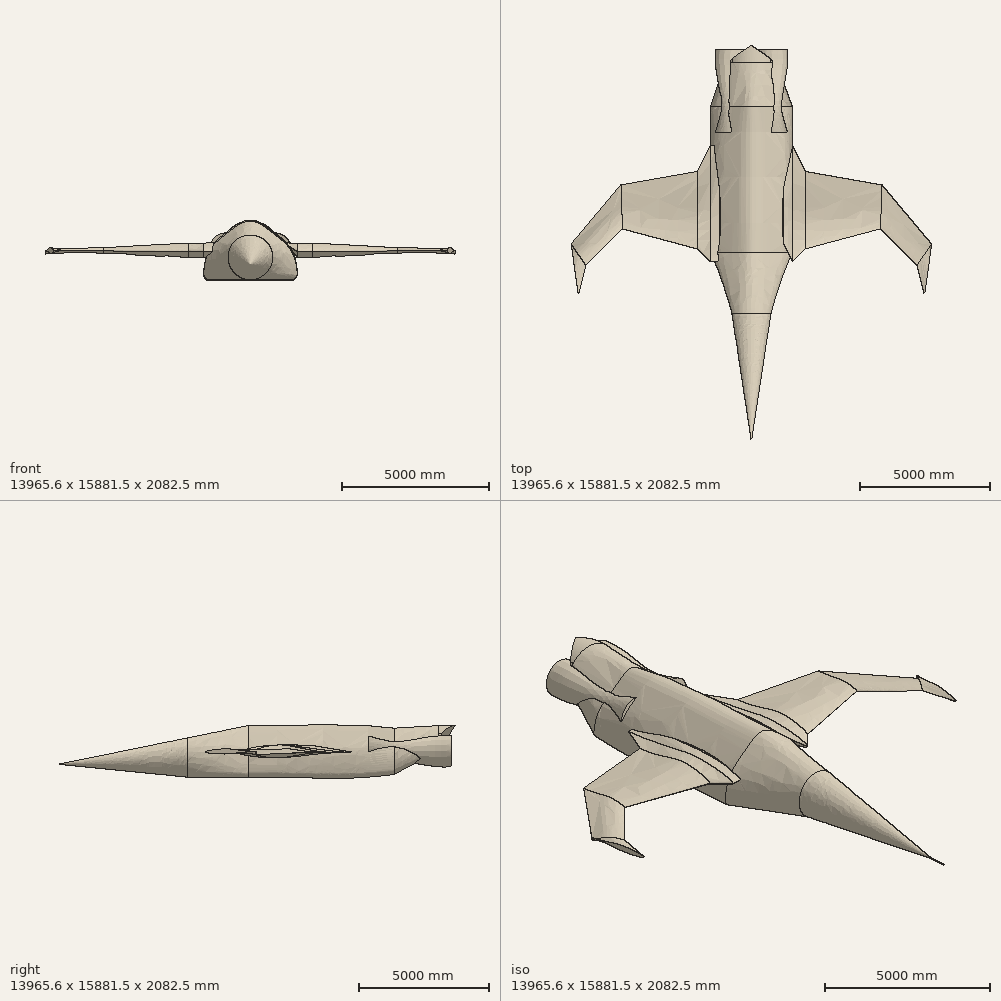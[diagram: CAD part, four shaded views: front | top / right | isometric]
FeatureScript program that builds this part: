
annotation { "Feature Type Name" : "Feature", "Feature Type Description" : "" }
export const myFeature = defineFeature(function(context is Context, id is Id, definition is map)
    precondition{}
    {
        {
            var Q0;
            Q0=qCreatedBy(makeId("Right.planeOp"),FACE);
            var sketch = newSketch(context, id + "F0", { "sketchPlane" : qUnion([Q0])});
            skLineSegment(sketch, "E0", {"start": v(0, 0) * mm, "end": v(-1750, 0) * mm});
            skLineSegment(sketch, "E1", {"start": v(-1750, 0) * mm, "end": v(-3500, 0) * mm});
            skLineSegment(sketch, "E2", {"start": v(-3500, 0) * mm, "end": v(-3500, -1000) * mm});
            skLineSegment(sketch, "E3", {"start": v(-3500, -1000) * mm, "end": v(-8500, -1000) * mm});
            skLineSegment(sketch, "E4", {"start": v(-8500, -1000) * mm, "end": v(-8500, -499.31) * mm});
            skLineSegment(sketch, "E5", {"start": v(-1151.4, 0) * mm, "end": v(-1151.4, 1000) * mm});
            skLineSegment(sketch, "E6", {"start": v(-1151.4, 1000) * mm, "end": v(-8500, -499.31) * mm});
            skLineSegment(sketch, "E7", {"start": v(-8500, -499.31) * mm, "end": v(-3500, -1000) * mm});
            skLineSegment(sketch, "E8", {"start": v(-3500, 0) * mm, "end": v(-3500, 520.82) * mm});
            skLineSegment(sketch, "E9", {"start": v(-8500, -499.31) * mm, "end": v(-8450, -499.31) * mm});
            skLineSegment(sketch, "E10", {"start": v(-8450, -499.31) * mm, "end": v(-8450, -489.1) * mm});
            skLineSegment(sketch, "E11", {"start": v(-8450, -499.31) * mm, "end": v(-8450, -504.32) * mm});
            skSolve(sketch);
        }
        {
            var Q0;
            Q0=sQuery(id+"F0.wireOp",EDGE,"E5");
            cPlane(context, id + "F1", {"entities" : qUnion([Q0]), "cplaneType" : CPlaneType.LINE_ANGLE, "offset" : 25 * mm, "angle" : 90 * degree, "oppositeDirection" : true, "width" : 150 * mm, "height" : 150 * mm});
        }
        {
            var Q0;
            Q0=qCreatedBy(id+"F1.planeOp",FACE);
            var sketch = newSketch(context, id + "F2", { "sketchPlane" : qUnion([Q0])});
            skLineSegment(sketch, "E12.top", {"start": v(-1394.2, -1000) * mm, "end": v(1394.2, -1000) * mm});
            skPoint(sketch, "E12.middle", {"position": v(0, 0) * mm});
            skFitSpline(sketch, "E13", {"points": [v(-1600, -1000) * mm, v(-848, 530) * mm, v(0, 1000) * mm, v(848, 530) * mm, v(1600, -1000) * mm], "startDerivative": vector(0, 10524.75) * mm, "endDerivative": vector(0, -10524.75) * mm});
            skArc(sketch, "E14", {"start": v(-735.27, 618.52) * mm, "mid": v(-1273.27, 435.52) * mm, "end": v(-1440.68, -107.53) * mm});
            skArc(sketch, "E15", {"start": v(1440.68, -107.53) * mm, "mid": v(1273.27, 435.52) * mm, "end": v(735.27, 618.52) * mm});
            skFitSpline(sketch, "E16.trimOffspring", {"points": [v(-1600, -1000) * mm, v(-848, 530) * mm, v(0, 1000) * mm, v(848, 530) * mm, v(1600, -1000) * mm], "startDerivative": vector(0, 10524.75) * mm, "endDerivative": vector(0, -10524.75) * mm});
            skFitSpline(sketch, "E17.trimOffspring", {"points": [v(-1600, -1000) * mm, v(-848, 530) * mm, v(0, 1000) * mm, v(848, 530) * mm, v(1600, -1000) * mm], "startDerivative": vector(0, 10524.75) * mm, "endDerivative": vector(0, -10524.75) * mm});
            skArc(sketch, "E18.filletArc", {"start": v(-1593.82, -787.83) * mm, "mid": v(-1539.85, -937.05) * mm, "end": v(-1394.2, -1000) * mm});
            skArc(sketch, "E19.filletArc", {"start": v(1394.2, -1000) * mm, "mid": v(1539.85, -937.05) * mm, "end": v(1593.82, -787.83) * mm});
            skSolve(sketch);
        }
        {
            var Q0;
            Q0=qCreatedBy(makeId("Front.planeOp"),FACE);
            var sketch = newSketch(context, id + "F3", { "sketchPlane" : qUnion([Q0])});
            skLineSegment(sketch, "E20.top", {"start": v(-1394.2, -1000) * mm, "end": v(1394.2, -1000) * mm});
            skPoint(sketch, "E20.middle", {"position": v(0, 0) * mm});
            skFitSpline(sketch, "E21", {"points": [v(-1600, -1000) * mm, v(-848, 530) * mm, v(0, 1000) * mm, v(848, 530) * mm, v(1600, -1000) * mm], "startDerivative": vector(0, 10524.75) * mm, "endDerivative": vector(0, -10524.75) * mm});
            skArc(sketch, "E22", {"start": v(-735.27, 618.52) * mm, "mid": v(-1273.27, 435.52) * mm, "end": v(-1440.68, -107.53) * mm});
            skArc(sketch, "E23", {"start": v(1440.68, -107.53) * mm, "mid": v(1273.27, 435.52) * mm, "end": v(735.27, 618.52) * mm});
            skFitSpline(sketch, "E24.trimOffspring", {"points": [v(-1600, -1000) * mm, v(-848, 530) * mm, v(0, 1000) * mm, v(848, 530) * mm, v(1600, -1000) * mm], "startDerivative": vector(0, 10524.75) * mm, "endDerivative": vector(0, -10524.75) * mm});
            skFitSpline(sketch, "E25.trimOffspring", {"points": [v(-1600, -1000) * mm, v(-848, 530) * mm, v(0, 1000) * mm, v(848, 530) * mm, v(1600, -1000) * mm], "startDerivative": vector(0, 10524.75) * mm, "endDerivative": vector(0, -10524.75) * mm});
            skArc(sketch, "E26.filletArc", {"start": v(-1593.82, -787.83) * mm, "mid": v(-1539.85, -937.05) * mm, "end": v(-1394.2, -1000) * mm});
            skArc(sketch, "E27.filletArc", {"start": v(1394.2, -1000) * mm, "mid": v(1539.85, -937.05) * mm, "end": v(1593.82, -787.83) * mm});
            skSolve(sketch);
        }
        {
            var Q0;
            Q0=qCreatedBy(makeId("Front.planeOp"),FACE);
            cPlane(context, id + "F4", {"entities" : qUnion([Q0]), "cplaneType" : CPlaneType.OFFSET, "offset" : 3500 * mm, "oppositeDirection" : true, "width" : 150 * mm, "height" : 150 * mm});
        }
        {
            var Q0;
            Q0=qCreatedBy(id+"F4.planeOp",FACE);
            var sketch = newSketch(context, id + "F5", { "sketchPlane" : qUnion([Q0])});
            skLineSegment(sketch, "E28.top", {"start": v(-1394.2, -1000) * mm, "end": v(1394.2, -1000) * mm});
            skPoint(sketch, "E28.middle", {"position": v(0, 0) * mm});
            skFitSpline(sketch, "E29", {"points": [v(-1600, -1000) * mm, v(-848, 530) * mm, v(0, 1000) * mm, v(848, 530) * mm, v(1600, -1000) * mm], "startDerivative": vector(0, 10524.75) * mm, "endDerivative": vector(0, -10524.75) * mm});
            skArc(sketch, "E30", {"start": v(-735.27, 618.52) * mm, "mid": v(-1273.27, 435.52) * mm, "end": v(-1440.68, -107.53) * mm});
            skArc(sketch, "E31", {"start": v(1440.68, -107.53) * mm, "mid": v(1273.27, 435.52) * mm, "end": v(735.27, 618.52) * mm});
            skFitSpline(sketch, "E32.trimOffspring", {"points": [v(-1600, -1000) * mm, v(-848, 530) * mm, v(0, 1000) * mm, v(848, 530) * mm, v(1600, -1000) * mm], "startDerivative": vector(0, 10524.75) * mm, "endDerivative": vector(0, -10524.75) * mm});
            skFitSpline(sketch, "E33.trimOffspring", {"points": [v(-1600, -1000) * mm, v(-848, 530) * mm, v(0, 1000) * mm, v(848, 530) * mm, v(1600, -1000) * mm], "startDerivative": vector(0, 10524.75) * mm, "endDerivative": vector(0, -10524.75) * mm});
            skArc(sketch, "E34.filletArc", {"start": v(-1593.82, -787.83) * mm, "mid": v(-1539.85, -937.05) * mm, "end": v(-1394.2, -1000) * mm});
            skArc(sketch, "E35.filletArc", {"start": v(1394.2, -1000) * mm, "mid": v(1539.85, -937.05) * mm, "end": v(1593.82, -787.83) * mm});
            skSolve(sketch);
        }
        {
            var Q0;
            Q0=qCreatedBy(makeId("Front.planeOp"),FACE);
            cPlane(context, id + "F6", {"entities" : qUnion([Q0]), "cplaneType" : CPlaneType.OFFSET, "offset" : 4500 * mm, "oppositeDirection" : true, "width" : 150 * mm, "height" : 150 * mm});
        }
        {
            var Q0;
            Q0=qCreatedBy(id+"F6.planeOp",FACE);
            var sketch = newSketch(context, id + "F7", { "sketchPlane" : qUnion([Q0])});
            skLineSegment(sketch, "E36.top", {"start": v(-1413.07, -900) * mm, "end": v(1413.07, -900) * mm});
            skPoint(sketch, "E36.middle", {"position": v(0, 0) * mm});
            skFitSpline(sketch, "E37", {"points": [v(-1600, -900) * mm, v(-784.42, 441.24) * mm, v(0, 900) * mm, v(784.42, 441.24) * mm, v(1600, -900) * mm], "startDerivative": vector(0, 9508.62) * mm, "endDerivative": vector(0, -9508.62) * mm});
            skArc(sketch, "E38", {"start": v(-719.25, 488.69) * mm, "mid": v(-1131.76, 394.84) * mm, "end": v(-1324.66, 18.33) * mm});
            skArc(sketch, "E39", {"start": v(1324.66, 18.33) * mm, "mid": v(1131.76, 394.84) * mm, "end": v(719.25, 488.69) * mm});
            skFitSpline(sketch, "E40.trimOffspring", {"points": [v(-1600, -900) * mm, v(-784.42, 441.24) * mm, v(0, 900) * mm, v(784.42, 441.24) * mm, v(1600, -900) * mm], "startDerivative": vector(0, 9508.62) * mm, "endDerivative": vector(0, -9508.62) * mm});
            skFitSpline(sketch, "E41.trimOffspring", {"points": [v(-1600, -900) * mm, v(-784.42, 441.24) * mm, v(0, 900) * mm, v(784.42, 441.24) * mm, v(1600, -900) * mm], "startDerivative": vector(0, 9508.62) * mm, "endDerivative": vector(0, -9508.62) * mm});
            skArc(sketch, "E42.filletArc", {"start": v(-1592.48, -705.43) * mm, "mid": v(-1545.4, -842.02) * mm, "end": v(-1413.07, -900) * mm});
            skArc(sketch, "E43.filletArc", {"start": v(1413.07, -900) * mm, "mid": v(1545.4, -842.02) * mm, "end": v(1592.48, -705.43) * mm});
            skLineSegment(sketch, "E44", {"start": v(-719.25, 488.69) * mm, "end": v(-1324.66, 18.33) * mm, "construction": true});
            skLineSegment(sketch, "E45", {"start": v(719.25, 488.69) * mm, "end": v(1324.66, 18.33) * mm, "construction": true});
            skSolve(sketch);
        }
        {
            var Q0;
            Q0=qCreatedBy(makeId("Front.planeOp"),FACE);
            cPlane(context, id + "F8", {"entities" : qUnion([Q0]), "cplaneType" : CPlaneType.OFFSET, "offset" : 6232.05 * mm, "oppositeDirection" : true, "width" : 150 * mm, "height" : 150 * mm});
        }
        {
            var Q0;
            Q0=qCreatedBy(id+"F8.planeOp",FACE);
            var sketch = newSketch(context, id + "F9", { "sketchPlane" : qUnion([Q0])});
            skArc(sketch, "E46", {"start": v(998.61, 52.63) * mm, "mid": v(0, 1000) * mm, "end": v(-998.61, 52.63) * mm});
            skLineSegment(sketch, "E47", {"start": v(0, 0) * mm, "end": v(-948.68, 0) * mm});
            skLineSegment(sketch, "E48", {"start": v(0, 0) * mm, "end": v(948.68, 0) * mm});
            skLineSegment(sketch, "E49", {"start": v(0, 1000) * mm, "end": v(0, 675) * mm, "construction": true});
            skLineSegment(sketch, "E50", {"start": v(0, 675) * mm, "end": v(-737.82, 675) * mm, "construction": true});
            skLineSegment(sketch, "E51", {"start": v(0, 675) * mm, "end": v(737.82, 675) * mm, "construction": true});
            skPoint(sketch, "E52.visualSharp", {"position": v(-1000, 0) * mm});
            skArc(sketch, "E52.filletArc", {"start": v(-998.61, 52.63) * mm, "mid": v(-984.96, 15.59) * mm, "end": v(-948.68, 0) * mm});
            skPoint(sketch, "E53.visualSharp", {"position": v(1000, 0) * mm});
            skArc(sketch, "E53.filletArc", {"start": v(948.68, 0) * mm, "mid": v(984.96, 15.59) * mm, "end": v(998.61, 52.63) * mm});
            skSolve(sketch);
        }
        {
            var Q0;
            Q0=makeQuery(id+"F2.imprint","IMPRINT",FACE,{"disambiguationData":[TD([[makeQuery(id+"F2.imprint","IMPRINT",EDGE,{"derivedFrom":sQuery(id+"F2.wireOp",EDGE,"E12.top")}),1.0]])]});
            var Q1;
            Q1=makeQuery(id+"F3.imprint","IMPRINT",FACE,{"disambiguationData":[TD([[makeQuery(id+"F3.imprint","IMPRINT",EDGE,{"derivedFrom":sQuery(id+"F3.wireOp",EDGE,"E20.top")}),1.0]])]});
            var Q2;
            Q2=makeQuery(id+"F5.imprint","IMPRINT",FACE,{"disambiguationData":[TD([[makeQuery(id+"F5.imprint","IMPRINT",EDGE,{"derivedFrom":sQuery(id+"F5.wireOp",EDGE,"E28.top")}),1.0]])]});
            var Q3;
            Q3=makeQuery(id+"F7.imprint","IMPRINT",FACE,{"disambiguationData":[TD([[makeQuery(id+"F7.imprint","IMPRINT",EDGE,{"derivedFrom":sQuery(id+"F7.wireOp",EDGE,"E36.top")}),1.0]])]});
            loft(context, id + "F10", {"sheetProfilesArray" : [{ "sheetProfileEntities" : qUnion([Q0]) }, { "sheetProfileEntities" : qUnion([Q1]) }, { "sheetProfileEntities" : qUnion([Q2]) }, { "sheetProfileEntities" : qUnion([Q3]) }]});
        }
        {
            var Q0;
            Q0=sQuery(id+"F7.wireOp",EDGE,"E44");
            var Q1;
            Q1=sQuery(id+"F9.wireOp",VERTEX,"E50.end");
            cPlane(context, id + "F11", {"entities" : qUnion([Q0, Q1]), "cplaneType" : CPlaneType.LINE_ANGLE, "offset" : 25 * mm, "angle" : 180 * degree, "width" : 150 * mm, "height" : 150 * mm});
        }
        {
            var Q0;
            Q0=qCreatedBy(id+"F11.planeOp",FACE);
            var sketch = newSketch(context, id + "F12", { "sketchPlane" : qUnion([Q0])});
            skLineSegment(sketch, "E54", {"start": v(-589.34, 4526.34) * mm, "end": v(-612.8, 6268.32) * mm});
            skLineSegment(sketch, "E55", {"start": v(-1354.08, 4472.19) * mm, "end": v(-612.8, 6268.32) * mm});
            skSolve(sketch);
        }
        {
            var Q0;
            Q0=sQuery(id+"F7.wireOp",EDGE,"E45");
            var Q1;
            Q1=sQuery(id+"F9.wireOp",VERTEX,"E51.end");
            cPlane(context, id + "F13", {"entities" : qUnion([Q0, Q1]), "cplaneType" : CPlaneType.LINE_ANGLE, "offset" : 25 * mm, "angle" : 0 * degree, "width" : 150 * mm, "height" : 150 * mm});
        }
        {
            var Q0;
            Q0=qCreatedBy(id+"F13.planeOp",FACE);
            var sketch = newSketch(context, id + "F14", { "sketchPlane" : qUnion([Q0])});
            skLineSegment(sketch, "E56", {"start": v(589.34, 4526.34) * mm, "end": v(612.8, 6268.32) * mm});
            skLineSegment(sketch, "E57", {"start": v(1354.08, 4472.19) * mm, "end": v(612.8, 6268.32) * mm});
            skSolve(sketch);
        }
        {
            var Q1;
            Q1=makeQuery(id+"F10.opLoft","CAP_FACE",FACE,{"disambiguationData":[OSD([makeQuery(id+"F7.imprint","IMPRINT",FACE,{"disambiguationData":[TD([[makeQuery(id+"F7.imprint","IMPRINT",EDGE,{"derivedFrom":sQuery(id+"F7.wireOp",EDGE,"E36.top")}),1.0]])]})])],"isStart":true});
            var Q2;
            Q2=makeQuery(id+"F9.imprint","IMPRINT",FACE,{"disambiguationData":[TD([[makeQuery(id+"F9.imprint","IMPRINT",EDGE,{"derivedFrom":sQuery(id+"F9.wireOp",EDGE,"E46")}),1.0]])]});
            var Q3;
            Q3=sQuery(id+"F12.wireOp",EDGE,"E54");
            var Q4;
            Q4=sQuery(id+"F14.wireOp",EDGE,"E56");
            loft(context, id + "F15", {"operationType" : NewBodyOperationType.ADD, "addGuides" : true, "sheetProfilesArray" : [{ "sheetProfileEntities" : qUnion([Q1]) }, { "sheetProfileEntities" : qUnion([Q2]) }], "guidesArray" : [{ "guideEntities" : qUnion([Q3]), "guideDerivativeType" : LoftGuideDerivativeType.DEFAULT, "guideDerivativeMagnitude" : 1 }, { "guideEntities" : qUnion([Q4]), "guideDerivativeType" : LoftGuideDerivativeType.DEFAULT, "guideDerivativeMagnitude" : 1 }]});
        }
        {
            var Q0;
            Q0=makeQuery(id+"F15.opLoft","CAP_FACE",FACE,{"disambiguationData":[OSD([makeQuery(id+"F9.imprint","IMPRINT",FACE,{"disambiguationData":[TD([[makeQuery(id+"F9.imprint","IMPRINT",EDGE,{"derivedFrom":sQuery(id+"F9.wireOp",EDGE,"E46")}),1.0]])]})])],"isStart":true});
            extrude(context, id + "F16", {"entities" : qUnion([Q0]), "operationType" : NewBodyOperationType.ADD, "depth" : 649.4 * mm, "offsetDistance" : 25 * mm});
        }
        {
            var Q0;
            Q0=qCreatedBy(makeId("Right.planeOp"),FACE);
            var sketch = newSketch(context, id + "F17", { "sketchPlane" : qUnion([Q0])});
            skLineSegment(sketch, "E58", {"start": v(0, 0) * mm, "end": v(4500, 0) * mm});
            skLineSegment(sketch, "E59", {"start": v(4500, 0) * mm, "end": v(6232.05, 0) * mm});
            skLineSegment(sketch, "E60", {"start": v(4500, 0) * mm, "end": v(4500, 1000) * mm});
            skLineSegment(sketch, "E61", {"start": v(4500, 1000) * mm, "end": v(6881.46, 1000) * mm});
            skLineSegment(sketch, "E62", {"start": v(6881.46, 1000) * mm, "end": v(6881.46, -1000) * mm});
            skLineSegment(sketch, "E63", {"start": v(6881.46, 1000) * mm, "end": v(6232.05, 0) * mm});
            skLineSegment(sketch, "E64", {"start": v(6232.05, 0) * mm, "end": v(5582.64, -1000) * mm});
            skLineSegment(sketch, "E65", {"start": v(5582.64, -1000) * mm, "end": v(6881.46, -1000) * mm});
            skSolve(sketch);
        }
        {
            var Q0;
            Q0=makeQuery(id+"F17.imprint","IMPRINT",FACE,{"disambiguationData":[TD([[makeQuery(id+"F17.imprint","IMPRINT",EDGE,{"derivedFrom":sQuery(id+"F17.wireOp",EDGE,"E62")}),-1.0]])]});
            var Q1;
            Q1=sQuery(id+"F17.wireOp",EDGE,"E61");
            revolve(context, id + "F18", {"operationType" : NewBodyOperationType.REMOVE, "entities" : qUnion([Q0]), "axis" : qUnion([Q1]), "revolveType" : RevolveType.SYMMETRIC, "oppositeDirection" : true, "angle" : 182 * degree});
        }
        {
            var Q0;
            Q0=qCreatedBy(id+"F1.planeOp",FACE);
            var sketch = newSketch(context, id + "F19", { "sketchPlane" : qUnion([Q0])});
            skLineSegment(sketch, "E66.top", {"start": v(-1394.2, -1000) * mm, "end": v(1394.2, -1000) * mm});
            skPoint(sketch, "E66.middle", {"position": v(0, 0) * mm});
            skFitSpline(sketch, "E67", {"points": [v(-1600, -1000) * mm, v(-848, 530) * mm, v(0, 1000) * mm, v(848, 530) * mm, v(1600, -1000) * mm], "startDerivative": vector(0, 10524.75) * mm, "endDerivative": vector(0, -10524.75) * mm});
            skArc(sketch, "E68.filletArc", {"start": v(-1593.82, -787.83) * mm, "mid": v(-1539.85, -937.05) * mm, "end": v(-1394.2, -1000) * mm});
            skArc(sketch, "E69.filletArc", {"start": v(1394.2, -1000) * mm, "mid": v(1539.85, -937.05) * mm, "end": v(1593.82, -787.83) * mm});
            skLineSegment(sketch, "E70", {"start": v(-1593.82, -787.83) * mm, "end": v(-1394.2, -1000) * mm, "construction": true});
            skLineSegment(sketch, "E71", {"start": v(1593.82, -787.83) * mm, "end": v(1394.2, -1000) * mm, "construction": true});
            skSolve(sketch);
        }
        {
            var Q0;
            Q0=qCreatedBy(makeId("Front.planeOp"),FACE);
            cPlane(context, id + "F20", {"entities" : qUnion([Q0]), "cplaneType" : CPlaneType.OFFSET, "offset" : 3500 * mm, "width" : 150 * mm, "height" : 150 * mm});
        }
        {
            var Q0;
            Q0=qCreatedBy(id+"F20.planeOp",FACE);
            var sketch = newSketch(context, id + "F21", { "sketchPlane" : qUnion([Q0])});
            skCircle(sketch, "E72", {"center": v(0, -239.59) * mm, "radius": 760.41 * mm});
            skLineSegment(sketch, "E73", {"start": v(0, -1000) * mm, "end": v(0, -800) * mm, "construction": true});
            skLineSegment(sketch, "E74", {"start": v(0, -800) * mm, "end": v(-513.97, -800) * mm, "construction": true});
            skLineSegment(sketch, "E75", {"start": v(0, -800) * mm, "end": v(513.97, -800) * mm, "construction": true});
            skSolve(sketch);
        }
        {
            var Q0;
            Q0=qCreatedBy(makeId("Front.planeOp"),FACE);
            cPlane(context, id + "F22", {"entities" : qUnion([Q0]), "cplaneType" : CPlaneType.OFFSET, "offset" : 8450 * mm, "width" : 150 * mm, "height" : 150 * mm});
        }
        {
            var Q0;
            Q0=qCreatedBy(id+"F22.planeOp",FACE);
            var sketch = newSketch(context, id + "F23", { "sketchPlane" : qUnion([Q0])});
            skCircle(sketch, "E76", {"center": v(0, -496.71) * mm, "radius": 7.6 * mm});
            skSolve(sketch);
        }
        {
            var Q0;
            Q0=sQuery(id+"F19.wireOp",EDGE,"E70");
            var Q1;
            Q1=sQuery(id+"F21.wireOp",VERTEX,"E74.end");
            cPlane(context, id + "F24", {"entities" : qUnion([Q0, Q1]), "cplaneType" : CPlaneType.LINE_ANGLE, "offset" : 25 * mm, "angle" : 0 * degree, "width" : 150 * mm, "height" : 150 * mm});
        }
        {
            var Q0;
            Q0=qCreatedBy(id+"F24.planeOp",FACE);
            var sketch = newSketch(context, id + "F25", { "sketchPlane" : qUnion([Q0])});
            skLineSegment(sketch, "E77", {"start": v(3032.27, -230.44) * mm, "end": v(558.11, 518.4) * mm});
            skLineSegment(sketch, "E78", {"start": v(3032.27, -230.44) * mm, "end": v(558.11, 227.09) * mm});
            skSolve(sketch);
        }
        {
            var Q0;
            Q0=sQuery(id+"F19.wireOp",EDGE,"E71");
            var Q1;
            Q1=sQuery(id+"F21.wireOp",VERTEX,"E75.end");
            cPlane(context, id + "F26", {"entities" : qUnion([Q0, Q1]), "cplaneType" : CPlaneType.LINE_ANGLE, "offset" : 25 * mm, "angle" : 180 * degree, "width" : 150 * mm, "height" : 150 * mm});
        }
        {
            var Q0;
            Q0=qCreatedBy(id+"F26.planeOp",FACE);
            var sketch = newSketch(context, id + "F27", { "sketchPlane" : qUnion([Q0])});
            skLineSegment(sketch, "E79", {"start": v(-3032.27, -230.44) * mm, "end": v(-558.11, 518.4) * mm});
            skLineSegment(sketch, "E80", {"start": v(-3032.27, -230.44) * mm, "end": v(-558.11, 227.09) * mm});
            skSolve(sketch);
        }
        {
            var Q1;
            Q1=makeQuery(id+"F19.imprint","IMPRINT",FACE,{"disambiguationData":[TD([[makeQuery(id+"F19.imprint","IMPRINT",EDGE,{"derivedFrom":sQuery(id+"F19.wireOp",EDGE,"E66.top")}),1.0]])]});
            var Q2;
            Q2=makeQuery(id+"F21.imprint","IMPRINT",FACE,{"disambiguationData":[TD([[makeQuery(id+"F21.imprint","IMPRINT",EDGE,{"derivedFrom":sQuery(id+"F21.wireOp",EDGE,"E72")}),1.0]])]});
            var Q3;
            Q3=sQuery(id+"F25.wireOp",EDGE,"E77");
            var Q4;
            Q4=sQuery(id+"F27.wireOp",EDGE,"E79");
            loft(context, id + "F28", {"operationType" : NewBodyOperationType.ADD, "addGuides" : true, "sheetProfilesArray" : [{ "sheetProfileEntities" : qUnion([Q1]) }, { "sheetProfileEntities" : qUnion([Q2]) }], "guidesArray" : [{ "guideEntities" : qUnion([Q3]), "guideDerivativeType" : LoftGuideDerivativeType.DEFAULT, "guideDerivativeMagnitude" : 1 }, { "guideEntities" : qUnion([Q4]), "guideDerivativeType" : LoftGuideDerivativeType.DEFAULT, "guideDerivativeMagnitude" : 1 }]});
        }
        {
            var Q1;
            Q1=makeQuery(id+"F28.opLoft","CAP_FACE",FACE,{"disambiguationData":[OSD([makeQuery(id+"F21.imprint","IMPRINT",FACE,{"disambiguationData":[TD([[makeQuery(id+"F21.imprint","IMPRINT",EDGE,{"derivedFrom":sQuery(id+"F21.wireOp",EDGE,"E72")}),1.0]])]})])],"isStart":true});
            var Q2;
            Q2=makeQuery(id+"F23.imprint","IMPRINT",FACE,{"disambiguationData":[TD([[makeQuery(id+"F23.imprint","IMPRINT",EDGE,{"derivedFrom":sQuery(id+"F23.wireOp",EDGE,"E76")}),1.0]])]});
            loft(context, id + "F29", {"operationType" : NewBodyOperationType.ADD, "sheetProfilesArray" : [{ "sheetProfileEntities" : qUnion([Q1]) }, { "sheetProfileEntities" : qUnion([Q2]) }]});
        }
        {
            var Q0;
            Q0=makeQuery(id+"F29.opLoft","CAP_FACE",FACE,{"disambiguationData":[OSD([makeQuery(id+"F23.imprint","IMPRINT",FACE,{"disambiguationData":[TD([[makeQuery(id+"F23.imprint","IMPRINT",EDGE,{"derivedFrom":sQuery(id+"F23.wireOp",EDGE,"E76")}),1.0]])]})])],"isStart":true});
            extrude(context, id + "F30", {"entities" : qUnion([Q0]), "operationType" : NewBodyOperationType.ADD, "depth" : 550 * mm, "offsetDistance" : 25 * mm});
        }
        {
            var Q0;
            Q0=qCreatedBy(makeId("Front.planeOp"),FACE);
            cPlane(context, id + "F31", {"entities" : qUnion([Q0]), "cplaneType" : CPlaneType.OFFSET, "offset" : 3500 * mm, "oppositeDirection" : true, "width" : 150 * mm, "height" : 150 * mm});
        }
        {
            var Q0;
            Q0=qCreatedBy(id+"F31.planeOp",FACE);
            var sketch = newSketch(context, id + "F32", { "sketchPlane" : qUnion([Q0])});
            skCircle(sketch, "E81", {"center": v(-800, 0) * mm, "radius": 600 * mm});
            skCircle(sketch, "E82", {"center": v(800, 0) * mm, "radius": 600 * mm});
            skSolve(sketch);
        }
        {
            var Q0;
            Q0=qCreatedBy(makeId("Front.planeOp"),FACE);
            cPlane(context, id + "F33", {"entities" : qUnion([Q0]), "cplaneType" : CPlaneType.OFFSET, "offset" : 4500 * mm, "oppositeDirection" : true, "width" : 150 * mm, "height" : 150 * mm});
        }
        {
            var Q0;
            Q0=qCreatedBy(id+"F33.planeOp",FACE);
            var sketch = newSketch(context, id + "F34", { "sketchPlane" : qUnion([Q0])});
            skCircle(sketch, "E83", {"center": v(-800, 0) * mm, "radius": 400 * mm});
            skCircle(sketch, "E84", {"center": v(800, 0) * mm, "radius": 400 * mm});
            skSolve(sketch);
        }
        {
            var Q0;
            Q0=qCreatedBy(makeId("Front.planeOp"),FACE);
            cPlane(context, id + "F35", {"entities" : qUnion([Q0]), "cplaneType" : CPlaneType.OFFSET, "offset" : 6232.05 * mm, "oppositeDirection" : true, "width" : 150 * mm, "height" : 150 * mm});
        }
        {
            var Q0;
            Q0=qCreatedBy(id+"F35.planeOp",FACE);
            var sketch = newSketch(context, id + "F36", { "sketchPlane" : qUnion([Q0])});
            skCircle(sketch, "E85", {"center": v(-800, 0) * mm, "radius": 600 * mm});
            skCircle(sketch, "E86", {"center": v(800, 0) * mm, "radius": 600 * mm});
            skSolve(sketch);
        }
        {
            var Q0;
            Q0=qCreatedBy(makeId("Front.planeOp"),FACE);
            cPlane(context, id + "F37", {"entities" : qUnion([Q0]), "cplaneType" : CPlaneType.OFFSET, "offset" : 6732.05 * mm, "oppositeDirection" : true, "width" : 150 * mm, "height" : 150 * mm});
        }
        {
            var Q0;
            Q0=qCreatedBy(id+"F37.planeOp",FACE);
            var sketch = newSketch(context, id + "F38", { "sketchPlane" : qUnion([Q0])});
            skCircle(sketch, "E87", {"center": v(-800, 0) * mm, "radius": 600 * mm});
            skCircle(sketch, "E88", {"center": v(800, 0) * mm, "radius": 600 * mm});
            skSolve(sketch);
        }
        {
            var Q0;
            Q0=makeQuery(id+"F32.imprint","IMPRINT",FACE,{"disambiguationData":[TD([[makeQuery(id+"F32.imprint","IMPRINT",EDGE,{"derivedFrom":sQuery(id+"F32.wireOp",EDGE,"E81")}),1.0]])]});
            var Q1;
            Q1=makeQuery(id+"F34.imprint","IMPRINT",FACE,{"disambiguationData":[TD([[makeQuery(id+"F34.imprint","IMPRINT",EDGE,{"derivedFrom":sQuery(id+"F34.wireOp",EDGE,"E83")}),1.0]])]});
            var Q2;
            Q2=makeQuery(id+"F36.imprint","IMPRINT",FACE,{"disambiguationData":[TD([[makeQuery(id+"F36.imprint","IMPRINT",EDGE,{"derivedFrom":sQuery(id+"F36.wireOp",EDGE,"E85")}),1.0]])]});
            var Q3;
            Q3=makeQuery(id+"F38.imprint","IMPRINT",FACE,{"disambiguationData":[TD([[makeQuery(id+"F38.imprint","IMPRINT",EDGE,{"derivedFrom":sQuery(id+"F38.wireOp",EDGE,"E87")}),1.0]])]});
            loft(context, id + "F39", {"sheetProfilesArray" : [{ "sheetProfileEntities" : qUnion([Q0]) }, { "sheetProfileEntities" : qUnion([Q1]) }, { "sheetProfileEntities" : qUnion([Q2]) }, { "sheetProfileEntities" : qUnion([Q3]) }]});
        }
        {
            var Q0;
            Q0=makeQuery(id+"F32.imprint","IMPRINT",FACE,{"disambiguationData":[TD([[makeQuery(id+"F32.imprint","IMPRINT",EDGE,{"derivedFrom":sQuery(id+"F32.wireOp",EDGE,"E82")}),1.0]])]});
            var Q1;
            Q1=makeQuery(id+"F34.imprint","IMPRINT",FACE,{"disambiguationData":[TD([[makeQuery(id+"F34.imprint","IMPRINT",EDGE,{"derivedFrom":sQuery(id+"F34.wireOp",EDGE,"E84")}),1.0]])]});
            var Q2;
            Q2=makeQuery(id+"F36.imprint","IMPRINT",FACE,{"disambiguationData":[TD([[makeQuery(id+"F36.imprint","IMPRINT",EDGE,{"derivedFrom":sQuery(id+"F36.wireOp",EDGE,"E86")}),1.0]])]});
            var Q3;
            Q3=makeQuery(id+"F38.imprint","IMPRINT",FACE,{"disambiguationData":[TD([[makeQuery(id+"F38.imprint","IMPRINT",EDGE,{"derivedFrom":sQuery(id+"F38.wireOp",EDGE,"E88")}),1.0]])]});
            loft(context, id + "F40", {"sheetProfilesArray" : [{ "sheetProfileEntities" : qUnion([Q0]) }, { "sheetProfileEntities" : qUnion([Q1]) }, { "sheetProfileEntities" : qUnion([Q2]) }, { "sheetProfileEntities" : qUnion([Q3]) }]});
        }
        {
            var Q0;
            Q0=qCreatedBy(makeId("Top.planeOp"),FACE);
            var sketch = newSketch(context, id + "F41", { "sketchPlane" : qUnion([Q0])});
            skLineSegment(sketch, "E89", {"start": v(0, 0) * mm, "end": v(-1250, 0) * mm});
            skLineSegment(sketch, "E90", {"start": v(-1250, 0) * mm, "end": v(-2100, 0) * mm});
            skLineSegment(sketch, "E91", {"start": v(-2100, 0) * mm, "end": v(-2100, -1000) * mm});
            skLineSegment(sketch, "E92", {"start": v(-2100, 0) * mm, "end": v(-2100, 2000) * mm});
            skLineSegment(sketch, "E93", {"start": v(-2100, -1000) * mm, "end": v(-4997.78, -223.54) * mm});
            skLineSegment(sketch, "E94", {"start": v(-2100, 2000) * mm, "end": v(-5054.42, 1479.06) * mm});
            skLineSegment(sketch, "E95", {"start": v(-4997.78, -223.54) * mm, "end": v(-5054.42, 1479.06) * mm});
            skLineSegment(sketch, "E96", {"start": v(-4997.78, -223.54) * mm, "end": v(-6412, -1637.76) * mm});
            skLineSegment(sketch, "E97", {"start": v(-5054.42, 1479.06) * mm, "end": v(-6982.79, -819.08) * mm});
            skLineSegment(sketch, "E98", {"start": v(-6412, -1637.76) * mm, "end": v(-6982.79, -819.08) * mm});
            skLineSegment(sketch, "E99", {"start": v(-6412, -1637.76) * mm, "end": v(-6704.44, -2799.61) * mm});
            skLineSegment(sketch, "E100", {"start": v(-6704.44, -2799.61) * mm, "end": v(-6982.79, -819.08) * mm});
            skLineSegment(sketch, "E101", {"start": v(0, 0) * mm, "end": v(1250, 0) * mm});
            skLineSegment(sketch, "E102", {"start": v(1250, 0) * mm, "end": v(2100, 0) * mm});
            skLineSegment(sketch, "E103", {"start": v(2100, 0) * mm, "end": v(2100, -1000) * mm});
            skLineSegment(sketch, "E104", {"start": v(2100, 0) * mm, "end": v(2100, 2000) * mm});
            skLineSegment(sketch, "E105", {"start": v(2100, -1000) * mm, "end": v(4997.78, -223.54) * mm});
            skLineSegment(sketch, "E106", {"start": v(2100, 2000) * mm, "end": v(5054.42, 1479.06) * mm});
            skLineSegment(sketch, "E107", {"start": v(4997.78, -223.54) * mm, "end": v(5054.42, 1479.06) * mm});
            skLineSegment(sketch, "E108", {"start": v(4997.78, -223.54) * mm, "end": v(6412, -1637.76) * mm});
            skLineSegment(sketch, "E109", {"start": v(5054.42, 1479.06) * mm, "end": v(6982.79, -819.08) * mm});
            skLineSegment(sketch, "E110", {"start": v(6412, -1637.76) * mm, "end": v(6982.79, -819.08) * mm});
            skLineSegment(sketch, "E111", {"start": v(6412, -1637.76) * mm, "end": v(6704.44, -2799.61) * mm});
            skLineSegment(sketch, "E112", {"start": v(6704.44, -2799.61) * mm, "end": v(6982.79, -819.08) * mm});
            skSolve(sketch);
        }
        {
            var Q0;
            Q0=qCreatedBy(makeId("Right.planeOp"),FACE);
            var sketch = newSketch(context, id + "F42", { "sketchPlane" : qUnion([Q0])});
            skFitSpline(sketch, "E113", {"points": [v(-1500, -50) * mm, v(0, 250) * mm, v(3000, -50) * mm, v(0, -250) * mm, v(-1500, -50) * mm]});
            skSolve(sketch);
        }
        {
            var Q0;
            Q0=qCreatedBy(makeId("Right.planeOp"),FACE);
            cPlane(context, id + "F43", {"entities" : qUnion([Q0]), "cplaneType" : CPlaneType.OFFSET, "offset" : 1600 * mm, "oppositeDirection" : true, "width" : 150 * mm, "height" : 150 * mm});
        }
        {
            var Q0;
            Q0=qCreatedBy(id+"F43.planeOp",FACE);
            var sketch = newSketch(context, id + "F44", { "sketchPlane" : qUnion([Q0])});
            skFitSpline(sketch, "E114", {"points": [v(-1500, -50) * mm, v(0, 250) * mm, v(3000, -50) * mm], "startDerivative": vector(0, 887.04) * mm, "endDerivative": vector(7705.35, -256.85) * mm});
            skFitSpline(sketch, "E115", {"points": [v(-1500, -50) * mm, v(0, -250) * mm, v(3000, -50) * mm], "startDerivative": vector(0, -722.87) * mm, "endDerivative": vector(7692.49, -256.42) * mm});
            skSolve(sketch);
        }
        {
            var Q0;
            Q0=qCreatedBy(makeId("Right.planeOp"),FACE);
            cPlane(context, id + "F45", {"entities" : qUnion([Q0]), "cplaneType" : CPlaneType.OFFSET, "offset" : 1600 * mm, "width" : 150 * mm, "height" : 150 * mm});
        }
        {
            var Q0;
            Q0=qCreatedBy(id+"F45.planeOp",FACE);
            var sketch = newSketch(context, id + "F46", { "sketchPlane" : qUnion([Q0])});
            skFitSpline(sketch, "E116", {"points": [v(-1500, -50) * mm, v(0, 250) * mm, v(3000, -50) * mm], "startDerivative": vector(0, 887.04) * mm, "endDerivative": vector(7705.35, -256.85) * mm});
            skFitSpline(sketch, "E117", {"points": [v(-1500, -50) * mm, v(0, -250) * mm, v(3000, -50) * mm], "startDerivative": vector(0, -722.87) * mm, "endDerivative": vector(7692.49, -256.42) * mm});
            skSolve(sketch);
        }
        {
            var Q0;
            Q0=qCreatedBy(makeId("Right.planeOp"),FACE);
            cPlane(context, id + "F47", {"entities" : qUnion([Q0]), "cplaneType" : CPlaneType.OFFSET, "offset" : 2100 * mm, "oppositeDirection" : true, "width" : 150 * mm, "height" : 150 * mm});
        }
        {
            var Q0;
            Q0=qCreatedBy(id+"F47.planeOp",FACE);
            var sketch = newSketch(context, id + "F48", { "sketchPlane" : qUnion([Q0])});
            skFitSpline(sketch, "E118", {"points": [v(-1000, -36) * mm, v(0, 250) * mm, v(2000, -36) * mm], "startDerivative": vector(0, 574.5) * mm, "endDerivative": vector(5152.5, -185.5) * mm});
            skFitSpline(sketch, "E119", {"points": [v(-1000, -36) * mm, v(0, -250) * mm, v(2000, -36) * mm], "startDerivative": vector(0, -699.11) * mm, "endDerivative": vector(5139.1, -185) * mm});
            skSolve(sketch);
        }
        {
            var Q0;
            Q0=qCreatedBy(makeId("Right.planeOp"),FACE);
            cPlane(context, id + "F49", {"entities" : qUnion([Q0]), "cplaneType" : CPlaneType.OFFSET, "offset" : 2100 * mm, "width" : 150 * mm, "height" : 150 * mm});
        }
        {
            var Q0;
            Q0=qCreatedBy(id+"F49.planeOp",FACE);
            var sketch = newSketch(context, id + "F50", { "sketchPlane" : qUnion([Q0])});
            skFitSpline(sketch, "E120", {"points": [v(-1000, -36) * mm, v(0, 250) * mm, v(2000, -36) * mm], "startDerivative": vector(0, 574.5) * mm, "endDerivative": vector(5152.5, -185.5) * mm});
            skFitSpline(sketch, "E121", {"points": [v(-1000, -36) * mm, v(0, -250) * mm, v(2000, -36) * mm], "startDerivative": vector(0, -699.11) * mm, "endDerivative": vector(5139.1, -185) * mm});
            skSolve(sketch);
        }
        {
            var Q0;
            Q0=sQuery(id+"F41.wireOp",EDGE,"E95");
            cPlane(context, id + "F51", {"entities" : qUnion([Q0]), "cplaneType" : CPlaneType.LINE_ANGLE, "offset" : 25 * mm, "angle" : 90 * degree, "oppositeDirection" : true, "width" : 150 * mm, "height" : 150 * mm});
        }
        {
            var Q0;
            Q0=qCreatedBy(id+"F51.planeOp",FACE);
            var sketch = newSketch(context, id + "F52", { "sketchPlane" : qUnion([Q0])});
            skFitSpline(sketch, "E122", {"points": [v(57.23, -18) * mm, v(-442.77, 100) * mm, v(-1646.3, -18) * mm], "startDerivative": vector(0, 311.71) * mm, "endDerivative": vector(-2981.97, -89.2) * mm});
            skFitSpline(sketch, "E123", {"points": [v(57.23, -18) * mm, v(-442.77, -100) * mm, v(-1646.3, -18) * mm], "startDerivative": vector(0, -370) * mm, "endDerivative": vector(-2975.3, -89) * mm});
            skSolve(sketch);
        }
        {
            var Q0;
            Q0=sQuery(id+"F41.wireOp",EDGE,"E107");
            cPlane(context, id + "F53", {"entities" : qUnion([Q0]), "cplaneType" : CPlaneType.LINE_ANGLE, "offset" : 25 * mm, "angle" : 90 * degree, "width" : 150 * mm, "height" : 150 * mm});
        }
        {
            var Q0;
            Q0=qCreatedBy(id+"F53.planeOp",FACE);
            var sketch = newSketch(context, id + "F54", { "sketchPlane" : qUnion([Q0])});
            skFitSpline(sketch, "E124", {"points": [v(-57.23, -18) * mm, v(442.77, 100) * mm, v(1646.3, -18) * mm], "startDerivative": vector(0, 311.71) * mm, "endDerivative": vector(2981.97, -89.2) * mm});
            skFitSpline(sketch, "E125", {"points": [v(-57.23, -18) * mm, v(442.77, -100) * mm, v(1646.3, -18) * mm], "startDerivative": vector(0, -370) * mm, "endDerivative": vector(2975.3, -89) * mm});
            skSolve(sketch);
        }
        {
            var Q0;
            Q0=sQuery(id+"F41.wireOp",EDGE,"E98");
            cPlane(context, id + "F55", {"entities" : qUnion([Q0]), "cplaneType" : CPlaneType.LINE_ANGLE, "offset" : 25 * mm, "angle" : 90 * degree, "oppositeDirection" : true, "width" : 150 * mm, "height" : 150 * mm});
        }
        {
            var Q0;
            Q0=qCreatedBy(id+"F55.planeOp",FACE);
            var sketch = newSketch(context, id + "F56", { "sketchPlane" : qUnion([Q0])});
            skFitSpline(sketch, "E126", {"points": [v(-2323.74, 0) * mm, v(-2822.75, 50) * mm, v(-3321.76, -125) * mm], "startDerivative": vector(-1017.94, 211.55) * mm, "endDerivative": vector(-978.27, -458.6) * mm});
            skFitSpline(sketch, "E127", {"points": [v(-2323.74, 0) * mm, v(-2822.75, -50) * mm, v(-3321.76, -125) * mm], "startDerivative": vector(-1000.33, -87.77) * mm, "endDerivative": vector(-995.7, -162.2) * mm});
            skSolve(sketch);
        }
        {
            var Q0;
            Q0=sQuery(id+"F41.wireOp",EDGE,"E110");
            cPlane(context, id + "F57", {"entities" : qUnion([Q0]), "cplaneType" : CPlaneType.LINE_ANGLE, "offset" : 25 * mm, "angle" : 90 * degree, "width" : 150 * mm, "height" : 150 * mm});
        }
        {
            var Q0;
            Q0=qCreatedBy(id+"F57.planeOp",FACE);
            var sketch = newSketch(context, id + "F58", { "sketchPlane" : qUnion([Q0])});
            skFitSpline(sketch, "E128", {"points": [v(2323.74, 0) * mm, v(2822.75, 50) * mm, v(3321.76, -125) * mm], "startDerivative": vector(1017.94, 211.55) * mm, "endDerivative": vector(978.27, -458.6) * mm});
            skFitSpline(sketch, "E129", {"points": [v(2323.74, 0) * mm, v(2822.75, -50) * mm, v(3321.76, -125) * mm], "startDerivative": vector(1000.33, -87.77) * mm, "endDerivative": vector(995.7, -162.2) * mm});
            skSolve(sketch);
        }
        {
            var Q0;
            Q0=sQuery(id+"F41.wireOp",EDGE,"E100");
            cPlane(context, id + "F59", {"entities" : qUnion([Q0]), "cplaneType" : CPlaneType.LINE_ANGLE, "offset" : 25 * mm, "angle" : 90 * degree, "oppositeDirection" : true, "width" : 150 * mm, "height" : 150 * mm});
        }
        {
            var Q0;
            Q0=qCreatedBy(id+"F59.planeOp",FACE);
            var sketch = newSketch(context, id + "F60", { "sketchPlane" : qUnion([Q0])});
            skFitSpline(sketch, "E130", {"points": [v(1839.3, -18) * mm, v(1039.3, 100) * mm, v(-160.7, -18) * mm], "startDerivative": vector(0, 273.2) * mm, "endDerivative": vector(-3274.07, -98.22) * mm});
            skFitSpline(sketch, "E131", {"points": [v(1839.3, -18) * mm, v(1039.3, -100) * mm, v(-160.7, -18) * mm], "startDerivative": vector(0, -323.44) * mm, "endDerivative": vector(-3271.82, -98.15) * mm});
            skSolve(sketch);
        }
        {
            var Q0;
            Q0=sQuery(id+"F41.wireOp",EDGE,"E112");
            cPlane(context, id + "F61", {"entities" : qUnion([Q0]), "cplaneType" : CPlaneType.LINE_ANGLE, "offset" : 25 * mm, "angle" : 90 * degree, "width" : 150 * mm, "height" : 150 * mm});
        }
        {
            var Q0;
            Q0=qCreatedBy(id+"F61.planeOp",FACE);
            var sketch = newSketch(context, id + "F62", { "sketchPlane" : qUnion([Q0])});
            skFitSpline(sketch, "E132", {"points": [v(-1839.3, -18) * mm, v(-1039.3, 100) * mm, v(160.7, -18) * mm], "startDerivative": vector(0, 273.2) * mm, "endDerivative": vector(3274.07, -98.22) * mm});
            skFitSpline(sketch, "E133", {"points": [v(-1839.3, -18) * mm, v(-1039.3, -100) * mm, v(160.7, -18) * mm], "startDerivative": vector(0, -323.44) * mm, "endDerivative": vector(3271.82, -98.15) * mm});
            skSolve(sketch);
        }
        {
            var Q0;
            Q0=qSketchRegion(id+"F42",true);
            extrude(context, id + "F63", {"entities" : qUnion([Q0]), "endBound" : BoundingType.SYMMETRIC, "depth" : 2500 * mm, "offsetDistance" : 25 * mm});
        }
        {
            var Q1;
            Q1=makeQuery(id+"F63.opExtrude","CAP_FACE",FACE,{"disambiguationData":[OSD([sQuery(id+"F42.wireOp",EDGE,"E113")])],"isStart":true});
            var Q2;
            {var subQ0=sQuery(id+"F44.wireOp",EDGE,"E114");Q2=makeQuery(id+"F44.imprint","IMPRINT",FACE,{"disambiguationData":[TD([[makeQuery(id+"F44.imprint","IMPRINT",EDGE,{"derivedFrom":subQ0}),-1.0]])]});}
            loft(context, id + "F64", {"operationType" : NewBodyOperationType.ADD, "sheetProfilesArray" : [{ "sheetProfileEntities" : qUnion([Q1]) }, { "sheetProfileEntities" : qUnion([Q2]) }]});
        }
        {
            var Q1;
            Q1=makeQuery(id+"F63.opExtrude","CAP_FACE",FACE,{"disambiguationData":[OSD([sQuery(id+"F42.wireOp",EDGE,"E113")])],"isStart":false});
            var Q2;
            {var subQ0=sQuery(id+"F46.wireOp",EDGE,"E116");Q2=makeQuery(id+"F46.imprint","IMPRINT",FACE,{"disambiguationData":[TD([[makeQuery(id+"F46.imprint","IMPRINT",EDGE,{"derivedFrom":subQ0}),-1.0]])]});}
            loft(context, id + "F65", {"operationType" : NewBodyOperationType.ADD, "sheetProfilesArray" : [{ "sheetProfileEntities" : qUnion([Q1]) }, { "sheetProfileEntities" : qUnion([Q2]) }]});
        }
        {
            var Q1;
            {var subQ0=sQuery(id+"F44.wireOp",EDGE,"E114");Q1=makeQuery(id+"F64.opLoft","CAP_FACE",FACE,{"disambiguationData":[OSD([makeQuery(id+"F44.imprint","IMPRINT",FACE,{"disambiguationData":[TD([[makeQuery(id+"F44.imprint","IMPRINT",EDGE,{"derivedFrom":subQ0}),-1.0]])]})])],"isStart":true});}
            var Q2;
            {var subQ0=sQuery(id+"F48.wireOp",EDGE,"E118");Q2=makeQuery(id+"F48.imprint","IMPRINT",FACE,{"disambiguationData":[TD([[makeQuery(id+"F48.imprint","IMPRINT",EDGE,{"derivedFrom":subQ0}),-1.0]])]});}
            loft(context, id + "F66", {"operationType" : NewBodyOperationType.ADD, "sheetProfilesArray" : [{ "sheetProfileEntities" : qUnion([Q1]) }, { "sheetProfileEntities" : qUnion([Q2]) }]});
        }
        {
            var Q1;
            {var subQ0=sQuery(id+"F46.wireOp",EDGE,"E116");Q1=makeQuery(id+"F65.opLoft","CAP_FACE",FACE,{"disambiguationData":[OSD([makeQuery(id+"F46.imprint","IMPRINT",FACE,{"disambiguationData":[TD([[makeQuery(id+"F46.imprint","IMPRINT",EDGE,{"derivedFrom":subQ0}),-1.0]])]})])],"isStart":true});}
            var Q2;
            {var subQ0=sQuery(id+"F50.wireOp",EDGE,"E120");Q2=makeQuery(id+"F50.imprint","IMPRINT",FACE,{"disambiguationData":[TD([[makeQuery(id+"F50.imprint","IMPRINT",EDGE,{"derivedFrom":subQ0}),-1.0]])]});}
            loft(context, id + "F67", {"operationType" : NewBodyOperationType.ADD, "sheetProfilesArray" : [{ "sheetProfileEntities" : qUnion([Q1]) }, { "sheetProfileEntities" : qUnion([Q2]) }]});
        }
        {
            var Q1;
            {var subQ0=sQuery(id+"F48.wireOp",EDGE,"E118");Q1=makeQuery(id+"F66.opLoft","CAP_FACE",FACE,{"disambiguationData":[OSD([makeQuery(id+"F48.imprint","IMPRINT",FACE,{"disambiguationData":[TD([[makeQuery(id+"F48.imprint","IMPRINT",EDGE,{"derivedFrom":subQ0}),-1.0]])]})])],"isStart":true});}
            var Q2;
            {var subQ0=sQuery(id+"F52.wireOp",EDGE,"E122");Q2=makeQuery(id+"F52.imprint","IMPRINT",FACE,{"disambiguationData":[TD([[makeQuery(id+"F52.imprint","IMPRINT",EDGE,{"derivedFrom":subQ0}),1.0]])]});}
            loft(context, id + "F68", {"operationType" : NewBodyOperationType.ADD, "sheetProfilesArray" : [{ "sheetProfileEntities" : qUnion([Q1]) }, { "sheetProfileEntities" : qUnion([Q2]) }]});
        }
        {
            var Q1;
            {var subQ0=sQuery(id+"F50.wireOp",EDGE,"E120");Q1=makeQuery(id+"F67.opLoft","CAP_FACE",FACE,{"disambiguationData":[OSD([makeQuery(id+"F50.imprint","IMPRINT",FACE,{"disambiguationData":[TD([[makeQuery(id+"F50.imprint","IMPRINT",EDGE,{"derivedFrom":subQ0}),-1.0]])]})])],"isStart":true});}
            var Q2;
            {var subQ0=sQuery(id+"F54.wireOp",EDGE,"E124");Q2=makeQuery(id+"F54.imprint","IMPRINT",FACE,{"disambiguationData":[TD([[makeQuery(id+"F54.imprint","IMPRINT",EDGE,{"derivedFrom":subQ0}),-1.0]])]});}
            loft(context, id + "F69", {"operationType" : NewBodyOperationType.ADD, "sheetProfilesArray" : [{ "sheetProfileEntities" : qUnion([Q1]) }, { "sheetProfileEntities" : qUnion([Q2]) }]});
        }
        {
            var Q1;
            {var subQ0=sQuery(id+"F52.wireOp",EDGE,"E122");Q1=makeQuery(id+"F68.opLoft","CAP_FACE",FACE,{"disambiguationData":[OSD([makeQuery(id+"F52.imprint","IMPRINT",FACE,{"disambiguationData":[TD([[makeQuery(id+"F52.imprint","IMPRINT",EDGE,{"derivedFrom":subQ0}),1.0]])]})])],"isStart":true});}
            var Q2;
            Q2=makeQuery(id+"F56.imprint","IMPRINT",FACE,{"disambiguationData":[TD([[makeQuery(id+"F56.imprint","IMPRINT",EDGE,{"derivedFrom":sQuery(id+"F56.wireOp",EDGE,"E126")}),1.0]])]});
            loft(context, id + "F70", {"operationType" : NewBodyOperationType.ADD, "sheetProfilesArray" : [{ "sheetProfileEntities" : qUnion([Q1]) }, { "sheetProfileEntities" : qUnion([Q2]) }]});
        }
        {
            var Q1;
            {var subQ0=sQuery(id+"F54.wireOp",EDGE,"E124");Q1=makeQuery(id+"F69.opLoft","CAP_FACE",FACE,{"disambiguationData":[OSD([makeQuery(id+"F54.imprint","IMPRINT",FACE,{"disambiguationData":[TD([[makeQuery(id+"F54.imprint","IMPRINT",EDGE,{"derivedFrom":subQ0}),-1.0]])]})])],"isStart":true});}
            var Q2;
            Q2=makeQuery(id+"F58.imprint","IMPRINT",FACE,{"disambiguationData":[TD([[makeQuery(id+"F58.imprint","IMPRINT",EDGE,{"derivedFrom":sQuery(id+"F58.wireOp",EDGE,"E128")}),-1.0]])]});
            loft(context, id + "F71", {"operationType" : NewBodyOperationType.ADD, "sheetProfilesArray" : [{ "sheetProfileEntities" : qUnion([Q1]) }, { "sheetProfileEntities" : qUnion([Q2]) }]});
        }
        {
            var Q1;
            Q1=makeQuery(id+"F70.opLoft","CAP_FACE",FACE,{"disambiguationData":[OSD([makeQuery(id+"F56.imprint","IMPRINT",FACE,{"disambiguationData":[TD([[makeQuery(id+"F56.imprint","IMPRINT",EDGE,{"derivedFrom":sQuery(id+"F56.wireOp",EDGE,"E126")}),1.0]])]})])],"isStart":true});
            var Q2;
            {var subQ0=sQuery(id+"F60.wireOp",EDGE,"E130");Q2=makeQuery(id+"F60.imprint","IMPRINT",FACE,{"disambiguationData":[TD([[makeQuery(id+"F60.imprint","IMPRINT",EDGE,{"derivedFrom":subQ0}),1.0]])]});}
            loft(context, id + "F72", {"operationType" : NewBodyOperationType.ADD, "sheetProfilesArray" : [{ "sheetProfileEntities" : qUnion([Q1]) }, { "sheetProfileEntities" : qUnion([Q2]) }]});
        }
        {
            var Q1;
            Q1=makeQuery(id+"F71.opLoft","CAP_FACE",FACE,{"disambiguationData":[OSD([makeQuery(id+"F58.imprint","IMPRINT",FACE,{"disambiguationData":[TD([[makeQuery(id+"F58.imprint","IMPRINT",EDGE,{"derivedFrom":sQuery(id+"F58.wireOp",EDGE,"E128")}),-1.0]])]})])],"isStart":true});
            var Q2;
            {var subQ0=sQuery(id+"F62.wireOp",EDGE,"E132");Q2=makeQuery(id+"F62.imprint","IMPRINT",FACE,{"disambiguationData":[TD([[makeQuery(id+"F62.imprint","IMPRINT",EDGE,{"derivedFrom":subQ0}),-1.0]])]});}
            loft(context, id + "F73", {"operationType" : NewBodyOperationType.ADD, "sheetProfilesArray" : [{ "sheetProfileEntities" : qUnion([Q1]) }, { "sheetProfileEntities" : qUnion([Q2]) }]});
        }
    });
